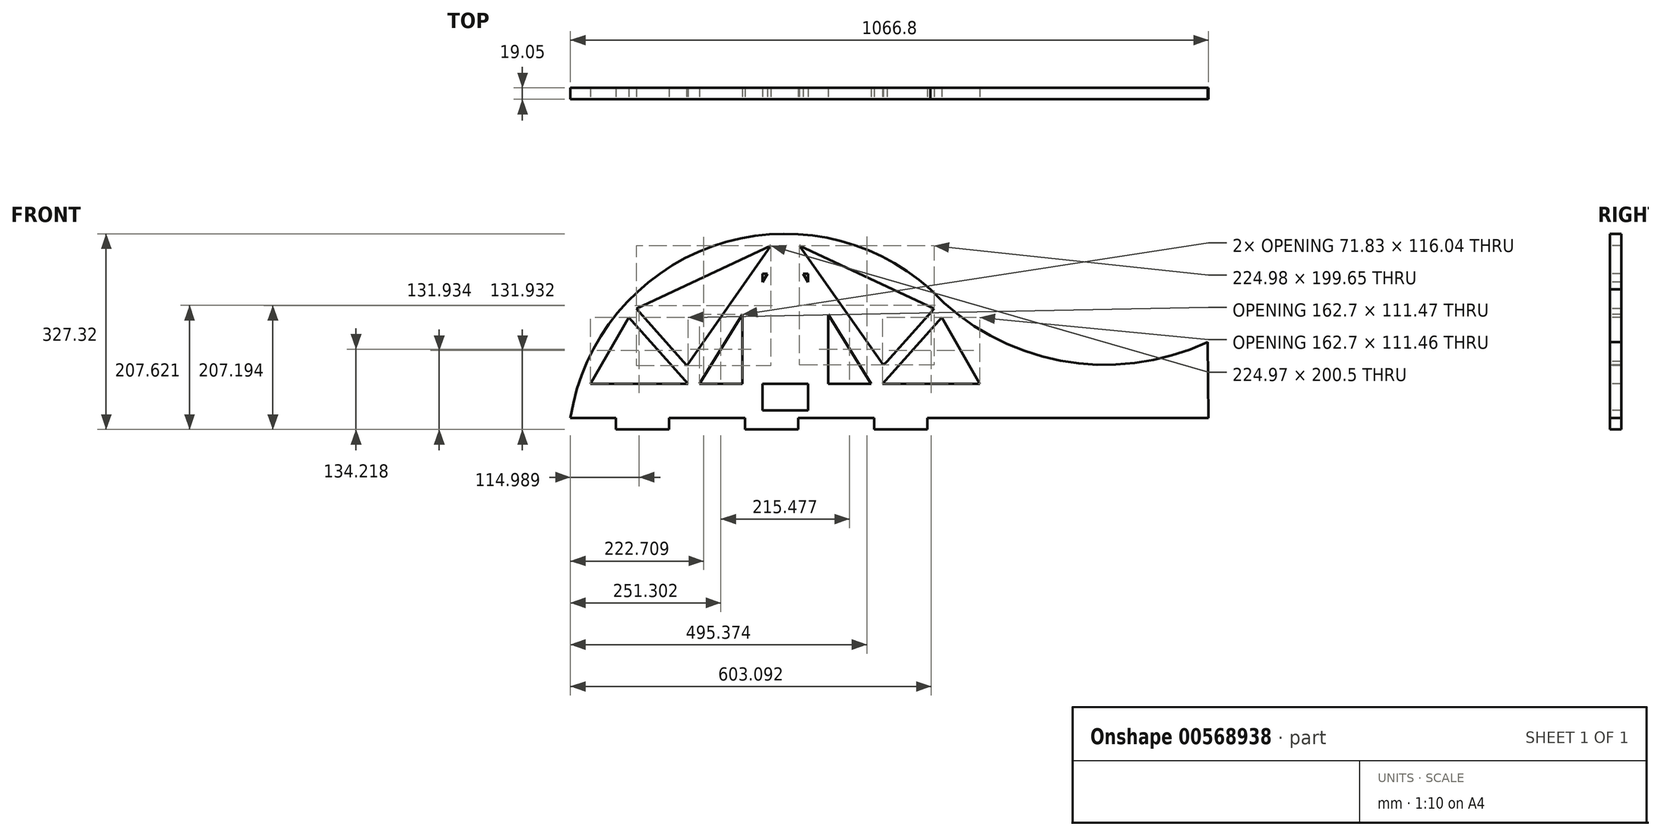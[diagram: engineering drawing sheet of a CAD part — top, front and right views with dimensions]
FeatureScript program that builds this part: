
annotation { "Feature Type Name" : "Feature", "Feature Type Description" : "" }
export const myFeature = defineFeature(function(context is Context, id is Id, definition is map)
    precondition{}
    {
        {
            var Q0;
            Q0=qCreatedBy(makeId("Front.planeOp"),FACE);
            var sketch = newSketch(context, id + "F0", { "sketchPlane" : qUnion([Q0])});
            skLineSegment(sketch, "E0", {"start": v(1219.75, -127) * mm, "end": v(152.95, -127) * mm});
            skPoint(sketch, "E1", {"position": v(512, -181.95) * mm});
            skArc(sketch, "E2", {"start": v(152.95, -127) * mm, "mid": v(389.49, 159.99) * mm, "end": v(754.45, 88.5) * mm});
            skArc(sketch, "E3", {"start": v(754.45, 88.5) * mm, "mid": v(971.96, -30.97) * mm, "end": v(1218.13, 0.3) * mm});
            skLineSegment(sketch, "E4", {"start": v(1218.13, 0.3) * mm, "end": v(1219.75, -127) * mm});
            skLineSegment(sketch, "E5", {"start": v(754.45, 88.5) * mm, "end": v(754.45, -127) * mm});
            skLineSegment(sketch, "E6", {"start": v(754.45, -127) * mm, "end": v(1219.75, -127) * mm});
            skSolve(sketch);
        }
        {
            var Q0;
            Q0=qSketchRegion(id+"F0",true);
            extrude(context, id + "F1", {"entities" : qUnion([Q0]), "depth" : 19.05 * mm, "offsetDistance" : 25.4 * mm});
        }
        {
            var Q0;
            Q0=makeQuery(id+"F1.opExtrude","CAP_FACE",FACE,{"disambiguationData":[OSD([sQuery(id+"F0.wireOp",EDGE,"E0"),sQuery(id+"F0.wireOp",EDGE,"E2"),sQuery(id+"F0.wireOp",EDGE,"E3"),sQuery(id+"F0.wireOp",EDGE,"E4"),sQuery(id+"F0.wireOp",EDGE,"E6")])],"isStart":false});
            var sketch = newSketch(context, id + "F2", { "sketchPlane" : qUnion([Q0])});
            skLineSegment(sketch, "E7", {"start": v(250.32, 41.62) * mm, "end": v(186.59, -69.85) * mm});
            skLineSegment(sketch, "E8", {"start": v(773.66, 41.61) * mm, "end": v(837.4, -69.85) * mm});
            skLineSegment(sketch, "E9", {"start": v(313.4, -69.85) * mm, "end": v(314.05, -69.85) * mm});
            skLineSegment(sketch, "E10", {"start": v(250.32, -127) * mm, "end": v(250.32, -69.85) * mm});
            skPoint(sketch, "E10.startSnap0", {"position": v(250.32, -69.85) * mm});
            skCircle(sketch, "E11", {"center": v(250.32, -98.43) * mm, "radius": 9.78 * mm});
            skLineSegment(sketch, "E12", {"start": v(250.32, 41.62) * mm, "end": v(349.29, -69.85) * mm});
            skLineSegment(sketch, "E13", {"start": v(773.66, 41.61) * mm, "end": v(674.7, -69.85) * mm});
            skLineSegment(sketch, "E14", {"start": v(456.77, 116.65) * mm, "end": v(398.77, 33.92) * mm});
            skLineSegment(sketch, "E15", {"start": v(275.35, 42.12) * mm, "end": v(321.76, -10.16) * mm});
            skLineSegment(sketch, "E16", {"start": v(398.77, 33.92) * mm, "end": v(349.29, -36.67) * mm});
            skLineSegment(sketch, "E17", {"start": v(321.76, -10.16) * mm, "end": v(345.3, -36.67) * mm});
            skLineSegment(sketch, "E18", {"start": v(345.3, -36.67) * mm, "end": v(347.07, -38.66) * mm});
            skLineSegment(sketch, "E19", {"start": v(349.29, -36.67) * mm, "end": v(347.58, -39.1) * mm});
            skLineSegment(sketch, "E20", {"start": v(347.58, -39.1) * mm, "end": v(347.07, -38.66) * mm});
            skLineSegment(sketch, "E21", {"start": v(275.35, 42.12) * mm, "end": v(263.17, 55.84) * mm});
            skLineSegment(sketch, "E22", {"start": v(456.77, 116.65) * mm, "end": v(488.15, 161.4) * mm});
            skLineSegment(sketch, "E23", {"start": v(488.15, 161.4) * mm, "end": v(263.17, 55.84) * mm});
            skLineSegment(sketch, "E24", {"start": v(558.16, 129.54) * mm, "end": v(618.05, 44.13) * mm});
            skLineSegment(sketch, "E25", {"start": v(738.86, 31.1) * mm, "end": v(696.51, -16.58) * mm});
            skLineSegment(sketch, "E26", {"start": v(696.51, -16.58) * mm, "end": v(738.86, 31.1) * mm});
            skLineSegment(sketch, "E27", {"start": v(558.16, 129.54) * mm, "end": v(535.84, 161.4) * mm});
            skLineSegment(sketch, "E28", {"start": v(738.86, 31.1) * mm, "end": v(760.81, 55.83) * mm});
            skLineSegment(sketch, "E29", {"start": v(760.81, 55.83) * mm, "end": v(535.84, 161.4) * mm});
            skLineSegment(sketch, "E30", {"start": v(696.51, -16.58) * mm, "end": v(682.48, -32.39) * mm});
            skLineSegment(sketch, "E31", {"start": v(618.05, 44.13) * mm, "end": v(675.8, -38.25) * mm});
            skLineSegment(sketch, "E32", {"start": v(675.8, -38.25) * mm, "end": v(682.48, -32.39) * mm});
            skLineSegment(sketch, "E33", {"start": v(186.59, -69.85) * mm, "end": v(349.29, -69.85) * mm});
            skLineSegment(sketch, "E34", {"start": v(368.34, -69.85) * mm, "end": v(655.64, -69.85) * mm});
            skLineSegment(sketch, "E35", {"start": v(674.7, -69.85) * mm, "end": v(837.4, -69.85) * mm});
            skLineSegment(sketch, "E36", {"start": v(512, 162.22) * mm, "end": v(368.34, -69.85) * mm});
            skLineSegment(sketch, "E37", {"start": v(512, 162.22) * mm, "end": v(655.64, -69.85) * mm});
            skSolve(sketch);
        }
        {
            var Q0;
            {var subQ3=sQuery(id+"F2.wireOp",EDGE,"E7");Q0=makeQuery(id+"F2.imprint","IMPRINT",FACE,{"disambiguationData":[TD([[makeQuery(id+"F2.imprint","IMPRINT",EDGE,{"derivedFrom":subQ3}),1.0]])]});}
            var Q1;
            Q1=makeQuery(id+"F2.imprint","IMPRINT",FACE,{"disambiguationData":[TD([[makeQuery(id+"F2.imprint","IMPRINT",EDGE,{"derivedFrom":sQuery(id+"F2.wireOp",EDGE,"E14")}),-1.0]])]});
            var Q2;
            Q2=makeQuery(id+"F2.imprint","IMPRINT",FACE,{"disambiguationData":[TD([[makeQuery(id+"F2.imprint","IMPRINT",EDGE,{"derivedFrom":sQuery(id+"F2.wireOp",EDGE,"E34")}),1.0]])]});
            var Q3;
            Q3=makeQuery(id+"F2.imprint","IMPRINT",FACE,{"disambiguationData":[TD([[makeQuery(id+"F2.imprint","IMPRINT",EDGE,{"derivedFrom":sQuery(id+"F2.wireOp",EDGE,"E24")}),1.0]])]});
            var Q4;
            Q4=makeQuery(id+"F2.imprint","IMPRINT",FACE,{"disambiguationData":[TD([[makeQuery(id+"F2.imprint","IMPRINT",EDGE,{"derivedFrom":sQuery(id+"F2.wireOp",EDGE,"E8")}),-1.0]])]});
            extrude(context, id + "F3", {"entities" : qUnion([Q0, Q1, Q2, Q3, Q4]), "operationType" : NewBodyOperationType.REMOVE, "oppositeDirection" : true, "depth" : 25.4 * mm, "offsetDistance" : 25.4 * mm});
        }
        {
            var Q0;
            {var subQ4=sQuery(id+"F2.wireOp",EDGE,"E7");Q0=makeQuery(id+"F2.imprint","IMPRINT",FACE,{"disambiguationData":[TD([[makeQuery(id+"F2.imprint","IMPRINT",EDGE,{"derivedFrom":subQ4}),-1.0]])]});}
            var sketch = newSketch(context, id + "F4", { "sketchPlane" : qUnion([Q0])});
            skLineSegment(sketch, "E38.0", {"start": v(1219.75, -127) * mm, "end": v(152.95, -127) * mm});
            skLineSegment(sketch, "E39.bottom", {"start": v(660.95, -127) * mm, "end": v(749.85, -127) * mm});
            skLineSegment(sketch, "E39.top", {"start": v(660.95, -146.05) * mm, "end": v(749.85, -146.05) * mm});
            skLineSegment(sketch, "E39.left", {"start": v(660.95, -127) * mm, "end": v(660.95, -146.05) * mm});
            skLineSegment(sketch, "E39.right", {"start": v(749.85, -127) * mm, "end": v(749.85, -146.05) * mm});
            skLineSegment(sketch, "E40.bottom", {"start": v(445.05, -127) * mm, "end": v(533.95, -127) * mm});
            skLineSegment(sketch, "E40.top", {"start": v(445.05, -146.05) * mm, "end": v(533.95, -146.05) * mm});
            skLineSegment(sketch, "E40.left", {"start": v(445.05, -127) * mm, "end": v(445.05, -146.05) * mm});
            skLineSegment(sketch, "E40.right", {"start": v(533.95, -127) * mm, "end": v(533.95, -146.05) * mm});
            skLineSegment(sketch, "E41.bottom", {"start": v(229.15, -127) * mm, "end": v(318.05, -127) * mm});
            skLineSegment(sketch, "E41.top", {"start": v(229.15, -146.05) * mm, "end": v(318.05, -146.05) * mm});
            skLineSegment(sketch, "E41.left", {"start": v(229.15, -127) * mm, "end": v(229.15, -146.05) * mm});
            skLineSegment(sketch, "E41.right", {"start": v(318.05, -127) * mm, "end": v(318.05, -146.05) * mm});
            skLineSegment(sketch, "E42.0.0", {"start": v(655.64, -69.85) * mm, "end": v(512, 162.22) * mm});
            skLineSegment(sketch, "E42.0.1", {"start": v(512, 162.22) * mm, "end": v(368.34, -69.85) * mm});
            skLineSegment(sketch, "E42.0.2", {"start": v(368.34, -69.85) * mm, "end": v(655.64, -69.85) * mm});
            skPoint(sketch, "E43.firstSnap0", {"position": v(512, -69.85) * mm});
            skLineSegment(sketch, "E43.bottom", {"start": v(512, -114.3) * mm, "end": v(473.9, -114.3) * mm});
            skLineSegment(sketch, "E43.top", {"start": v(512, 114.3) * mm, "end": v(473.9, 114.3) * mm});
            skLineSegment(sketch, "E43.left", {"start": v(512, -114.3) * mm, "end": v(512, 114.3) * mm});
            skLineSegment(sketch, "E43.right", {"start": v(473.9, -114.3) * mm, "end": v(473.9, 114.3) * mm});
            skLineSegment(sketch, "E44.bottom", {"start": v(512, -114.3) * mm, "end": v(550.1, -114.3) * mm});
            skLineSegment(sketch, "E44.top", {"start": v(512, 114.3) * mm, "end": v(550.1, 114.3) * mm});
            skLineSegment(sketch, "E44.right", {"start": v(550.1, -114.3) * mm, "end": v(550.1, 114.3) * mm});
            skLineSegment(sketch, "E45.0.0", {"start": v(275.35, 42.12) * mm, "end": v(321.76, -10.16) * mm});
            skLineSegment(sketch, "E45.0.1", {"start": v(321.76, -10.16) * mm, "end": v(345.3, -36.67) * mm});
            skLineSegment(sketch, "E45.0.2", {"start": v(345.3, -36.67) * mm, "end": v(347.07, -38.66) * mm});
            skLineSegment(sketch, "E45.0.3", {"start": v(347.07, -38.66) * mm, "end": v(347.58, -39.1) * mm});
            skLineSegment(sketch, "E45.0.4", {"start": v(347.58, -39.1) * mm, "end": v(349.29, -36.67) * mm});
            skLineSegment(sketch, "E45.0.5", {"start": v(349.29, -36.67) * mm, "end": v(398.77, 33.92) * mm});
            skLineSegment(sketch, "E45.0.6", {"start": v(398.77, 33.92) * mm, "end": v(456.77, 116.65) * mm});
            skLineSegment(sketch, "E45.0.7", {"start": v(456.77, 116.65) * mm, "end": v(488.15, 161.4) * mm});
            skLineSegment(sketch, "E45.0.8", {"start": v(488.15, 161.4) * mm, "end": v(263.17, 55.84) * mm});
            skLineSegment(sketch, "E45.0.9", {"start": v(263.17, 55.84) * mm, "end": v(275.35, 42.12) * mm});
            skLineSegment(sketch, "E46.0.0", {"start": v(682.48, -32.39) * mm, "end": v(696.51, -16.58) * mm});
            skLineSegment(sketch, "E46.0.1", {"start": v(696.51, -16.58) * mm, "end": v(738.86, 31.1) * mm});
            skLineSegment(sketch, "E46.0.2", {"start": v(738.86, 31.1) * mm, "end": v(760.81, 55.83) * mm});
            skLineSegment(sketch, "E46.0.3", {"start": v(760.81, 55.83) * mm, "end": v(535.84, 161.4) * mm});
            skLineSegment(sketch, "E46.0.4", {"start": v(535.84, 161.4) * mm, "end": v(558.16, 129.54) * mm});
            skLineSegment(sketch, "E46.0.5", {"start": v(558.16, 129.54) * mm, "end": v(618.05, 44.13) * mm});
            skLineSegment(sketch, "E46.0.6", {"start": v(618.05, 44.13) * mm, "end": v(675.8, -38.25) * mm});
            skLineSegment(sketch, "E46.0.7", {"start": v(675.8, -38.25) * mm, "end": v(682.48, -32.39) * mm});
            skPoint(sketch, "E47.oppositeSnap0", {"position": v(440.16, 46.19) * mm});
            skLineSegment(sketch, "E47.bottom", {"start": v(473.9, 100.67) * mm, "end": v(445.57, 100.67) * mm});
            skLineSegment(sketch, "E47.top", {"start": v(473.9, -69.85) * mm, "end": v(440.16, -69.85) * mm});
            skLineSegment(sketch, "E47.left", {"start": v(473.9, 100.67) * mm, "end": v(473.9, -69.85) * mm});
            skLineSegment(sketch, "E47.right", {"start": v(440.16, 92.96) * mm, "end": v(440.16, -69.85) * mm});
            skLineSegment(sketch, "E48", {"start": v(445.57, 100.67) * mm, "end": v(440.16, 92.96) * mm});
            skPoint(sketch, "E49.oppositeSnap0", {"position": v(583.82, 46.19) * mm});
            skLineSegment(sketch, "E49.bottom", {"start": v(550.1, 100.67) * mm, "end": v(578.4, 100.67) * mm});
            skLineSegment(sketch, "E49.top", {"start": v(550.1, -69.85) * mm, "end": v(583.82, -69.85) * mm});
            skLineSegment(sketch, "E49.left", {"start": v(550.1, 100.67) * mm, "end": v(550.1, -69.85) * mm});
            skLineSegment(sketch, "E49.right", {"start": v(583.82, 92.96) * mm, "end": v(583.82, -69.85) * mm});
            skLineSegment(sketch, "E50", {"start": v(578.4, 100.67) * mm, "end": v(583.82, 92.96) * mm});
            skSolve(sketch);
        }
        {
            var Q0;
            Q0=qSketchRegion(id+"F4",true);
            extrude(context, id + "F5", {"entities" : qUnion([Q0]), "operationType" : NewBodyOperationType.ADD, "oppositeDirection" : true, "depth" : 19.05 * mm, "offsetDistance" : 25.4 * mm});
        }
        {
            var Q0;
            {var subQ7=sQuery(id+"F4.wireOp",EDGE,"E47.left");Q0=makeQuery(id+"F4.imprint","IMPRINT",FACE,{"disambiguationData":[TD([[makeQuery(id+"F4.imprint","IMPRINT",EDGE,{"derivedFrom":subQ7}),1.0]])]});}
            var Q1;
            {var subQ5=sQuery(id+"F4.wireOp",EDGE,"E49.left");Q1=makeQuery(id+"F4.imprint","IMPRINT",FACE,{"disambiguationData":[TD([[makeQuery(id+"F4.imprint","IMPRINT",EDGE,{"derivedFrom":subQ5}),-1.0]])]});}
            var Q2;
            {var subQ0=sQuery(id+"F4.wireOp",EDGE,"E43.right");var subQ3=sQuery(id+"F4.wireOp",EDGE,"E43.top");var subQ5=makeQuery(id+"F4.imprint","INTERSECT",VERTEX,{"derivedFrom":[subQ3,subQ0]});Q2=makeQuery(id+"F4.imprint","IMPRINT",FACE,{"disambiguationData":[TD([[makeQuery(id+"F4.imprint","IMPRINT",EDGE,{"disambiguationData":[TD([[subQ5,1.0]])],"derivedFrom":subQ3}),1.0]])]});}
            var Q3;
            {var subQ0=sQuery(id+"F4.wireOp",EDGE,"E44.right");var subQ3=sQuery(id+"F4.wireOp",EDGE,"E44.top");var subQ5=makeQuery(id+"F4.imprint","INTERSECT",VERTEX,{"derivedFrom":[subQ3,subQ0]});Q3=makeQuery(id+"F4.imprint","IMPRINT",FACE,{"disambiguationData":[TD([[makeQuery(id+"F4.imprint","IMPRINT",EDGE,{"disambiguationData":[TD([[subQ5,1.0]])],"derivedFrom":subQ3}),-1.0]])]});}
            var Q4;
            {var subQ0=sQuery(id+"F4.wireOp",EDGE,"E42.0.2");var subQ1=sQuery(id+"F4.wireOp",EDGE,"E42.0.1");var subQ2=makeQuery(id+"F4.imprint","INTERSECT",VERTEX,{"derivedFrom":[subQ1,subQ0]});Q4=makeQuery(id+"F4.imprint","IMPRINT",FACE,{"disambiguationData":[TD([[makeQuery(id+"F4.imprint","IMPRINT",EDGE,{"disambiguationData":[TD([[subQ2,1.0]])],"derivedFrom":subQ1}),1.0]])]});}
            var Q5;
            {var subQ0=sQuery(id+"F4.wireOp",EDGE,"E42.0.2");var subQ1=sQuery(id+"F4.wireOp",EDGE,"E42.0.0");var subQ2=makeQuery(id+"F4.imprint","INTERSECT",VERTEX,{"derivedFrom":[subQ1,subQ0]});Q5=makeQuery(id+"F4.imprint","IMPRINT",FACE,{"disambiguationData":[TD([[makeQuery(id+"F4.imprint","IMPRINT",EDGE,{"disambiguationData":[TD([[subQ2,1.0]])],"derivedFrom":subQ1}),-1.0]])]});}
            var Q6;
            Q6=makeQuery(id+"F4.imprint","IMPRINT",FACE,{"disambiguationData":[TD([[makeQuery(id+"F4.imprint","IMPRINT",EDGE,{"derivedFrom":sQuery(id+"F4.wireOp",EDGE,"E45.0.0")}),1.0]])]});
            var Q7;
            Q7=makeQuery(id+"F4.imprint","IMPRINT",FACE,{"disambiguationData":[TD([[makeQuery(id+"F4.imprint","IMPRINT",EDGE,{"derivedFrom":sQuery(id+"F4.wireOp",EDGE,"E46.0.0")}),-1.0]])]});
            var Q8;
            {var subQ5=sQuery(id+"F4.wireOp",EDGE,"E44.bottom");Q8=makeQuery(id+"F4.imprint","IMPRINT",FACE,{"disambiguationData":[TD([[makeQuery(id+"F4.imprint","IMPRINT",EDGE,{"derivedFrom":subQ5}),1.0]])]});}
            var Q9;
            {var subQ5=sQuery(id+"F4.wireOp",EDGE,"E43.bottom");Q9=makeQuery(id+"F4.imprint","IMPRINT",FACE,{"disambiguationData":[TD([[makeQuery(id+"F4.imprint","IMPRINT",EDGE,{"derivedFrom":subQ5}),-1.0]])]});}
            extrude(context, id + "F6", {"entities" : qUnion([Q0, Q1, Q2, Q3, Q4, Q5, Q6, Q7, Q8, Q9]), "operationType" : NewBodyOperationType.REMOVE, "oppositeDirection" : true, "depth" : 25.4 * mm, "offsetDistance" : 25.4 * mm});
        }
    });
